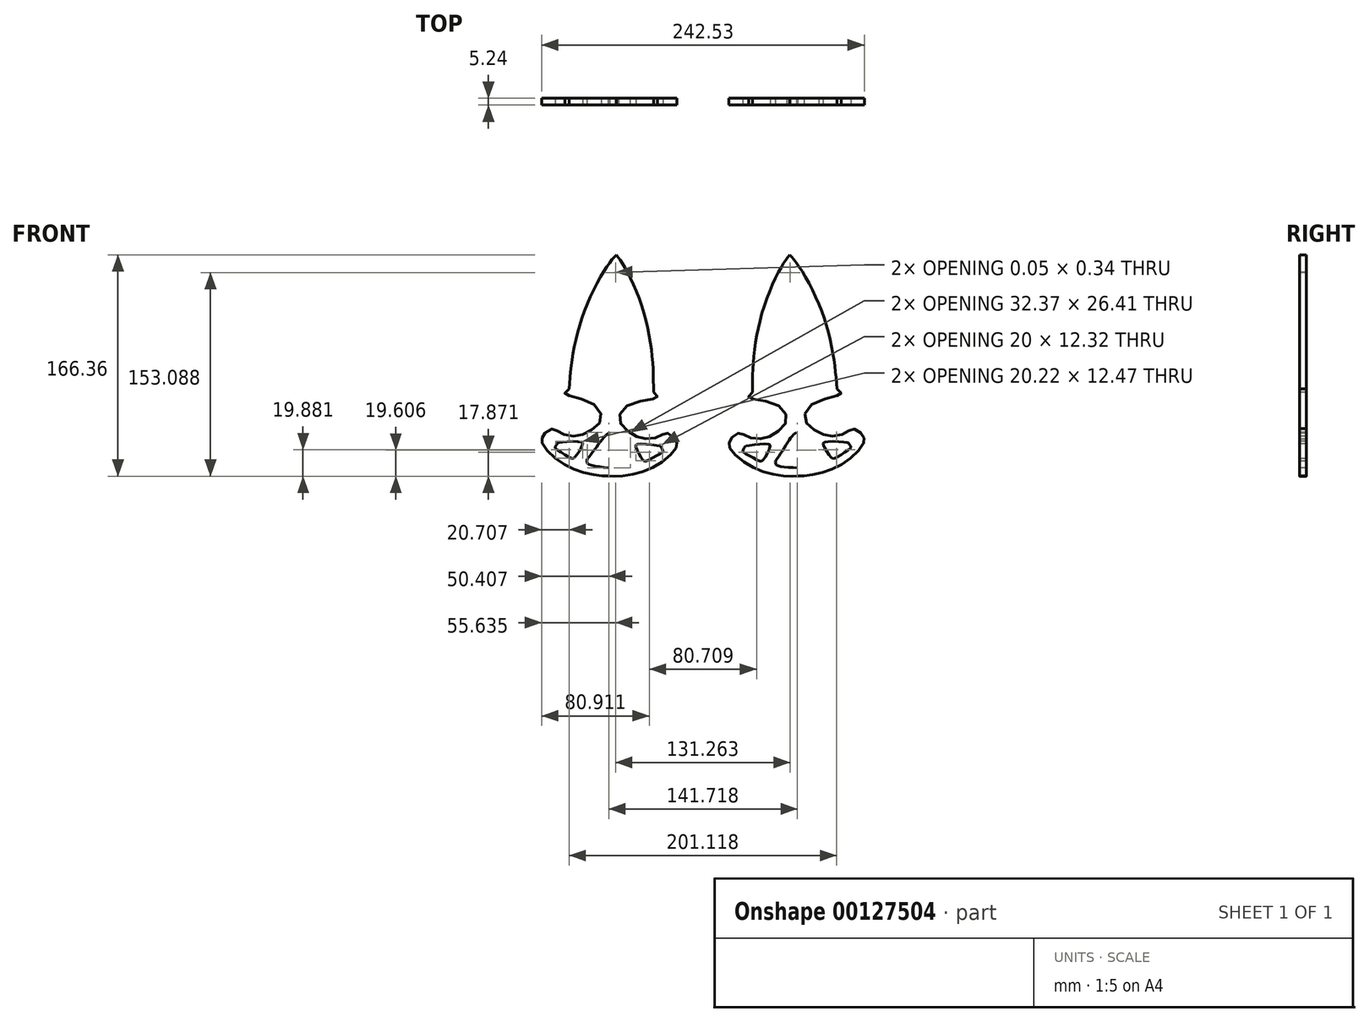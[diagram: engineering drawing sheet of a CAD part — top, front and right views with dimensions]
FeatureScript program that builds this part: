
annotation { "Feature Type Name" : "Feature", "Feature Type Description" : "" }
export const myFeature = defineFeature(function(context is Context, id is Id, definition is map)
    precondition{}
    {
        {
            var Q0;
            Q0=qCreatedBy(makeId("Front.planeOp"),FACE);
            var sketch = newSketch(context, id + "F0", { "sketchPlane" : qUnion([Q0])});
            skLineSegment(sketch, "E0", {"start": v(-36.1, 35.89) * mm, "end": v(-42.24, -130.1) * mm, "construction": true});
            skFitSpline(sketch, "E1", {"points": [v(-42.24, -130.1) * mm, v(-47.26, -130.1) * mm, v(-58.47, -128.22) * mm, v(-71.82, -123.39) * mm, v(-84.78, -114.3) * mm, v(-91.94, -105.01) * mm, v(-91.94, -101.92) * mm, v(-89.42, -97.85) * mm, v(-83.23, -94.76) * mm, v(-79.36, -97.08) * mm, v(-68.92, -100.37) * mm, v(-57.7, -97.47) * mm, v(-47.64, -88.18) * mm, v(-53.83, -75.8) * mm, v(-73.56, -69.42) * mm, v(-74.72, -68.07) * mm, v(-71.63, -64.97) * mm, v(-56.15, -60.14) * mm, v(-54.6, -52.4) * mm, v(-45.7, 0) * mm, v(-36.58, 22.79) * mm, v(-36.6, 22.45) * mm], "startDerivative": vector(-135.7, -6.17) * mm, "endDerivative": vector(-8.88, -56.25) * mm});
            skFitSpline(sketch, "E2", {"points": [v(-79.25, -105.02) * mm, v(-80.51, -105.75) * mm, v(-82.1, -108.68) * mm, v(-81.33, -109.77) * mm, v(-70.63, -116.65) * mm, v(-67.46, -116.44) * mm, v(-61.56, -107.09) * mm, v(-62.1, -104.93) * mm, v(-79.25, -105.02) * mm]});
            skFitSpline(sketch, "E3", {"points": [v(-41.04, -97.66) * mm, v(-44.2, -99.96) * mm, v(-50.26, -107.56) * mm, v(-56.79, -116.16) * mm, v(-58.1, -118.08) * mm, v(-57.7, -120.77) * mm, v(-42.02, -124.07) * mm], "startDerivative": vector(-24.04, -14.58) * mm, "endDerivative": vector(80.7, -7.27) * mm});
            skFitSpline(sketch, "E4.MirrorCS", {"points": [v(-42.24, -130.1) * mm, v(-37.25, -130.47) * mm, v(-25.92, -129.43) * mm, v(-12.25, -125.6) * mm, v(1.34, -117.48) * mm, v(9.17, -108.75) * mm, v(9.4, -105.67) * mm, v(7.19, -101.43) * mm, v(1.25, -97.89) * mm, v(-2.78, -99.92) * mm, v(-13.44, -102.42) * mm, v(-24.42, -98.7) * mm, v(-33.76, -88.7) * mm, v(-26.67, -76.8) * mm, v(-6.53, -71.9) * mm, v(-5.27, -70.64) * mm, v(-8.12, -67.32) * mm, v(-23.2, -61.36) * mm, v(-24.17, -53.53) * mm, v(-29.17, -0.61) * mm, v(-36.58, 22.79) * mm, v(-36.6, 22.45) * mm], "startDerivative": vector(134.87, -16.19) * mm, "endDerivative": vector(4.7, -56.75) * mm});
            skFitSpline(sketch, "E5.MirrorC", {"points": [v(-3.48, -107.82) * mm, v(-2.28, -108.65) * mm, v(-0.92, -111.68) * mm, v(-1.77, -112.72) * mm, v(-12.94, -118.78) * mm, v(-16.09, -118.34) * mm, v(-21.28, -108.58) * mm, v(-20.59, -106.47) * mm, v(-3.48, -107.82) * mm]});
            skFitSpline(sketch, "E6.MirrorCS", {"points": [v(-41.04, -97.66) * mm, v(-38.07, -100.2) * mm, v(-32.58, -108.22) * mm, v(-26.7, -117.27) * mm, v(-25.55, -119.29) * mm, v(-26.13, -121.94) * mm, v(-42.02, -124.07) * mm], "startDerivative": vector(22.9, -16.32) * mm, "endDerivative": vector(-81.01, -1.28) * mm});
            skFitSpline(sketch, "E7", {"points": [v(-71.63, -64.97) * mm, v(-68.76, -39.12) * mm, v(-58.36, -1.92) * mm, v(-42.22, 28.44) * mm, v(-36.1, 35.89) * mm], "startDerivative": vector(7.77, 98.41) * mm, "endDerivative": vector(36.25, 39.03) * mm});
            skFitSpline(sketch, "E8.MirrorCS", {"points": [v(-8.12, -67.32) * mm, v(-9.08, -41.33) * mm, v(-16.69, -3.47) * mm, v(-30.54, 28) * mm, v(-36.1, 35.89) * mm], "startDerivative": vector(-0.47, 98.72) * mm, "endDerivative": vector(-33.26, 41.6) * mm});
            skLineSegment(sketch, "E9", {"start": v(-85.98, -105.02) * mm, "end": v(2.92, -105.02) * mm, "construction": true});
            skLineSegment(sketch, "E10", {"start": v(29.05, 29.58) * mm, "end": v(29.05, -132.17) * mm, "construction": true});
            skFitSpline(sketch, "E11.MirrorCS", {"points": [v(66.22, -67.32) * mm, v(67.17, -41.33) * mm, v(74.78, -3.47) * mm, v(88.63, 28) * mm, v(94.19, 35.89) * mm], "startDerivative": vector(0.47, 98.72) * mm, "endDerivative": vector(33.26, 41.6) * mm});
            skFitSpline(sketch, "E12.MirrorCS", {"points": [v(100.34, -130.1) * mm, v(95.34, -130.47) * mm, v(84.01, -129.43) * mm, v(70.35, -125.6) * mm, v(56.75, -117.48) * mm, v(48.93, -108.75) * mm, v(48.7, -105.67) * mm, v(50.9, -101.43) * mm, v(56.85, -97.89) * mm, v(60.88, -99.92) * mm, v(71.54, -102.42) * mm, v(82.5, -98.7) * mm, v(91.85, -88.7) * mm, v(84.76, -76.8) * mm, v(64.62, -71.9) * mm, v(63.36, -70.64) * mm, v(66.22, -67.32) * mm, v(81.3, -61.36) * mm, v(82.26, -53.53) * mm, v(87.26, -0.61) * mm, v(94.67, 22.79) * mm, v(94.69, 22.45) * mm], "startDerivative": vector(-134.87, -16.19) * mm, "endDerivative": vector(-4.7, -56.75) * mm});
            skFitSpline(sketch, "E13.MirrorCS", {"points": [v(100.34, -130.1) * mm, v(105.35, -130.1) * mm, v(116.57, -128.22) * mm, v(129.91, -123.39) * mm, v(142.87, -114.3) * mm, v(150.03, -105.01) * mm, v(150.03, -101.92) * mm, v(147.51, -97.85) * mm, v(141.32, -94.76) * mm, v(137.46, -97.08) * mm, v(127.01, -100.37) * mm, v(115.8, -97.47) * mm, v(105.73, -88.18) * mm, v(111.92, -75.8) * mm, v(131.65, -69.42) * mm, v(132.81, -68.07) * mm, v(129.72, -64.97) * mm, v(114.25, -60.14) * mm, v(112.7, -52.4) * mm, v(103.8, 0) * mm, v(94.67, 22.79) * mm, v(94.69, 22.45) * mm], "startDerivative": vector(135.7, -6.17) * mm, "endDerivative": vector(8.88, -56.25) * mm});
            skLineSegment(sketch, "E14.MirrorCS", {"start": v(94.19, 35.89) * mm, "end": v(100.34, -130.1) * mm, "construction": true});
            skFitSpline(sketch, "E15.MirrorCS", {"points": [v(66.22, -67.32) * mm, v(67.17, -41.33) * mm, v(74.78, -3.47) * mm, v(88.63, 28) * mm, v(94.19, 35.89) * mm], "startDerivative": vector(0.47, 98.72) * mm, "endDerivative": vector(33.26, 41.6) * mm});
            skFitSpline(sketch, "E16.MirrorC", {"points": [v(61.58, -107.82) * mm, v(60.37, -108.65) * mm, v(59, -111.68) * mm, v(59.86, -112.72) * mm, v(71.03, -118.78) * mm, v(74.18, -118.34) * mm, v(79.37, -108.58) * mm, v(78.68, -106.47) * mm, v(61.58, -107.82) * mm]});
            skFitSpline(sketch, "E17.MirrorCS", {"points": [v(99.14, -97.66) * mm, v(96.16, -100.2) * mm, v(90.67, -108.22) * mm, v(84.8, -117.27) * mm, v(83.64, -119.29) * mm, v(84.22, -121.94) * mm, v(100.11, -124.07) * mm], "startDerivative": vector(-22.9, -16.32) * mm, "endDerivative": vector(81.01, -1.28) * mm});
            skFitSpline(sketch, "E18.MirrorCS", {"points": [v(99.14, -97.66) * mm, v(102.3, -99.96) * mm, v(108.36, -107.56) * mm, v(114.88, -116.16) * mm, v(116.18, -118.08) * mm, v(115.8, -120.77) * mm, v(100.11, -124.07) * mm], "startDerivative": vector(24.04, -14.58) * mm, "endDerivative": vector(-80.7, -7.27) * mm});
            skFitSpline(sketch, "E19.MirrorC", {"points": [v(137.34, -105.02) * mm, v(138.6, -105.75) * mm, v(140.19, -108.68) * mm, v(139.42, -109.77) * mm, v(128.72, -116.65) * mm, v(125.55, -116.44) * mm, v(119.66, -107.09) * mm, v(120.18, -104.93) * mm, v(137.34, -105.02) * mm]});
            skFitSpline(sketch, "E20.MirrorCS", {"points": [v(129.72, -64.97) * mm, v(126.85, -39.12) * mm, v(116.45, -1.92) * mm, v(100.32, 28.44) * mm, v(94.19, 35.89) * mm], "startDerivative": vector(-7.77, 98.41) * mm, "endDerivative": vector(-36.25, 39.03) * mm});
            skSolve(sketch);
        }
        {
            var Q0;
            Q0 = qSketchRegion(id + "F0", true);
            extrude(context, id + "F1", {"entities" : qUnion([Q0]), "endBound" : BoundingType.SYMMETRIC, "oppositeDirection" : true, "depth" : 5.24 * mm});
        }
    });
